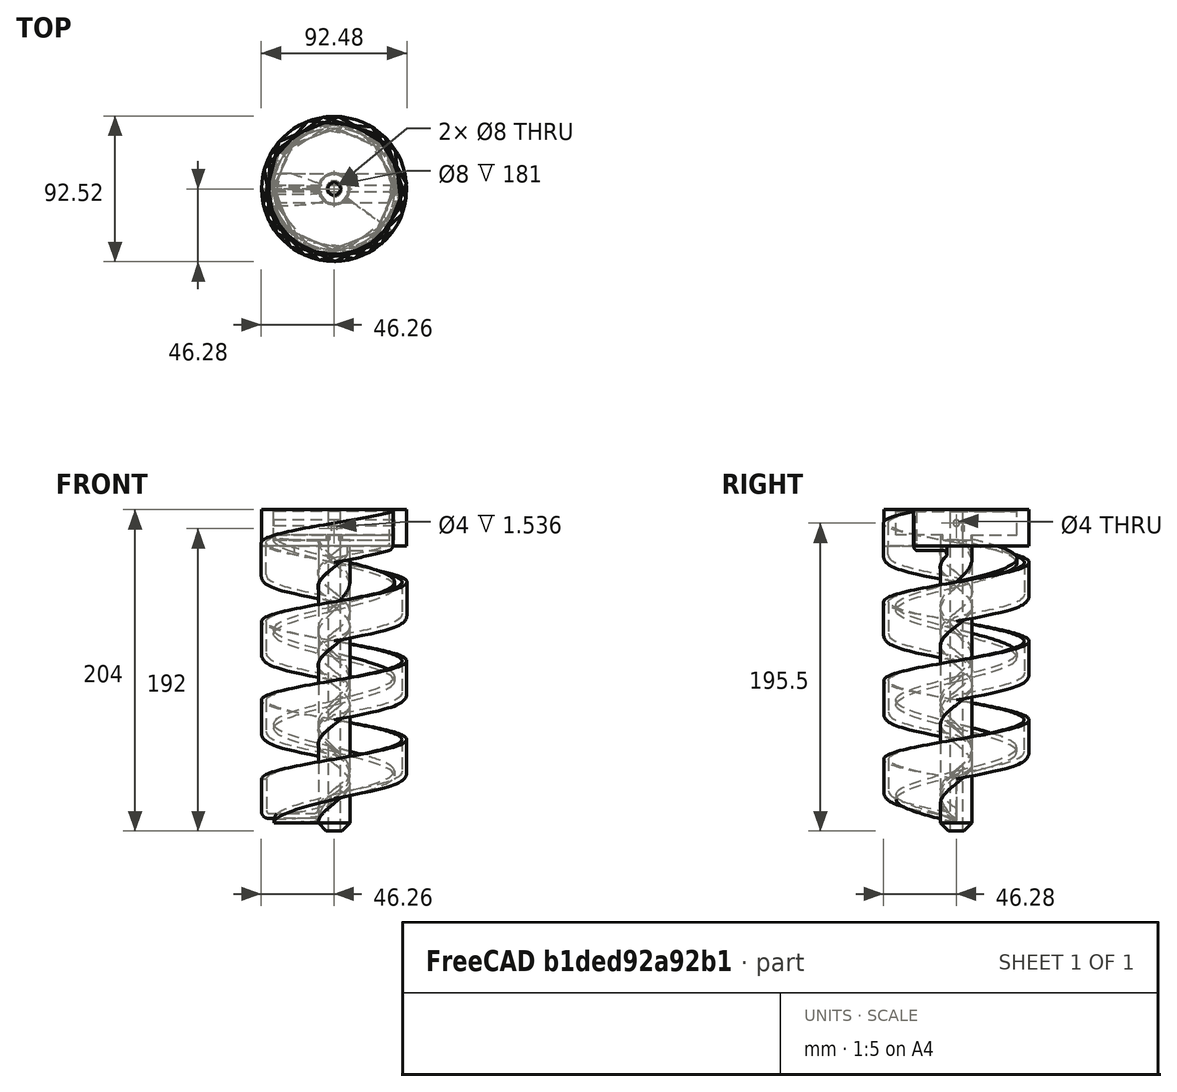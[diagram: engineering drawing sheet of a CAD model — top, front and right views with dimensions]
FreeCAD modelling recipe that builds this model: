
FCSTD DOCUMENT  (FreeCAD 1.1R14555 (Git shallow))
Label: Body - 1.3
License: All rights reserved
LicenseURL: https://en.wikipedia.org/wiki/All_rights_reserved
objects: Sketcher::SketchObject×12, PartDesign::Pad×6, PartDesign::Chamfer×5, PartDesign::Pocket×5, PartDesign::AdditiveHelix×2, PartDesign::Body×2, App::Point×2, PartDesign::Fillet×1
note: 83 computed .brp shape members not serialized (recipe doc carries the construction recipe); baked Part::Feature solids carry a one-line shape summary decoded from their .brp

FEATURE [Sketcher::SketchObject] Sketch
  ArcFitTolerance = 1e-06
  AttachmentSupport = -> [XY_Plane]
  ExternalTypes = [0]
  FullyConstrained = true
  MakeInternals = false
  MapMode = 5
  sketch-geometry (1):
    g0: Circle CenterX=0 CenterY=0 CenterZ=0 NormalX=0 NormalY=0 NormalZ=1 AngleXU=0 Radius=10
  constraints (2):
    c: Coincident(g0,g-1)
    c: Diameter(g0) = 20
FEATURE [PartDesign::Pad] Pad
  Direction = (0,0,1)
  Length = 200
  Length2 = 10
  Profile = -> Sketch
  ReferenceAxis = -> Sketch [N_Axis]
  Refine = true
  SideType = 0
  Suppressed = false
  Type = 0
  Type2 = 0
FEATURE [PartDesign::Chamfer] Chamfer
  Angle = 45
  Base = -> Pad [Edge2]
  BaseFeature = -> Pad
  ChamferType = 0
  FlipDirection = false
  Refine = true
  Size = 5
  Size2 = 1
  SupportTransform = false
  Suppressed = false
  UseAllEdges = false
FEATURE [Sketcher::SketchObject] Sketch001
  ArcFitTolerance = 1e-06
  AttachmentSupport = -> [XZ_Plane]
  ExternalGeometry = -> [Chamfer]
  ExternalTypes = [0]
  FullyConstrained = true
  MakeInternals = false
  MapMode = 5
  Placement = pos=(0,0,0) rot=(1,0,0;1.5708rad)
  expr: Constraints[11] = 77 / 2 - 0.3
  sketch-geometry (4):
    g0: LineSegment StartX=-38.2 StartY=8 StartZ=0 EndX=-38.2 EndY=5 EndZ=0
    g1: LineSegment StartX=-38.2 StartY=5 StartZ=0 EndX=0 EndY=5 EndZ=0
    g2: LineSegment StartX=0 StartY=5 StartZ=0 EndX=0 EndY=8 EndZ=0
    g3: LineSegment StartX=0 StartY=8 StartZ=0 EndX=-38.2 EndY=8 EndZ=0
  constraints (12):
    c: Coincident(g0,g1)
    c: Coincident(g1,g2)
    c: Coincident(g2,g3)
    c: Coincident(g3,g0)
    c: Vertical(g0)
    c: Vertical(g2)
    c: Horizontal(g1)
    c: Horizontal(g3)
    c: PointOnObject(g1,g-2)
    c: Horizontal(g0,g-3)
    c: DistanceY(g0,g0) = 3
    c: DistanceX(g1,g1) = 38.2
FEATURE [PartDesign::AdditiveHelix] AdditiveHelix
  Angle = 0.1
  Axis = (0,2e-16,1)
  Base = (0,0,0)
  BaseFeature = -> Chamfer
  Growth = 0.10472
  HasBeenEdited = true
  Height = 180
  LeftHanded = false
  Mode = 0
  Outside = false
  Pitch = 60
  Profile = -> Sketch001
  ReferenceAxis = -> Sketch001 [V_Axis]
  Refine = true
  Suppressed = false
  Tolerance = 0.1
  Turns = 3
FEATURE [Sketcher::SketchObject] Sketch002
  ArcFitTolerance = 1e-06
  AttachmentSupport = -> [Chamfer]
  ExternalTypes = [0]
  FullyConstrained = true
  MakeInternals = false
  MapMode = 5
  Placement = pos=(0,0,200) rot=(0,0,1;0rad)
  sketch-geometry (1):
    g0: Circle CenterX=0 CenterY=0 CenterZ=0 NormalX=0 NormalY=0 NormalZ=1 AngleXU=0 Radius=38.5
  constraints (2):
    c: Coincident(g0,g-1)
    c: Diameter(g0) = 77
FEATURE [PartDesign::Chamfer] Chamfer001
  Angle = 45
  Base = -> AdditiveHelix [Edge12]
  BaseFeature = -> AdditiveHelix
  ChamferType = 0
  FlipDirection = false
  Refine = true
  Size = 2.99
  Size2 = 1
  SupportTransform = false
  Suppressed = false
  UseAllEdges = false
FEATURE [PartDesign::Chamfer] Chamfer002
  Angle = 45
  Base = -> Chamfer001 [Edge12]
  BaseFeature = -> Chamfer001
  ChamferType = 0
  FlipDirection = false
  Refine = true
  Size = 4
  Size2 = 1
  SupportTransform = false
  Suppressed = false
  UseAllEdges = false
FEATURE [PartDesign::Chamfer] Chamfer003
  Angle = 45
  Base = -> Chamfer002 [Edge13]
  BaseFeature = -> Chamfer002
  ChamferType = 0
  FlipDirection = false
  Refine = true
  Size = 4
  Size2 = 1
  SupportTransform = false
  Suppressed = false
  UseAllEdges = false
FEATURE [PartDesign::Pad] Pad001
  BaseFeature = -> Chamfer003
  Direction = (0,0,1)
  Length = 3
  Length2 = 10
  Profile = -> Sketch002
  ReferenceAxis = -> Sketch002 [N_Axis]
  Refine = true
  SideType = 0
  Suppressed = false
  Type = 0
  Type2 = 0
FEATURE [Sketcher::SketchObject] Sketch003
  ArcFitTolerance = 1e-06
  AttachmentSupport = -> [Pad001]
  ExternalTypes = [0]
  FullyConstrained = true
  MakeInternals = false
  MapMode = 5
  Placement = pos=(0,0,200) rot=(1,0,0;3.14159rad)
  sketch-geometry (1):
    g0: Circle CenterX=0 CenterY=0 CenterZ=0 NormalX=0 NormalY=0 NormalZ=1 AngleXU=0 Radius=38.5
  constraints (2):
    c: Coincident(g0,g-1)
    c: Diameter(g0) = 77
FEATURE [PartDesign::Pad] Pad002
  BaseFeature = -> Pad001
  Direction = (0,0,-1)
  Length = 12
  Length2 = 10
  Profile = -> Sketch003
  ReferenceAxis = -> Sketch003 [N_Axis]
  Refine = true
  SideType = 0
  Suppressed = false
  Type = 0
  Type2 = 0
FEATURE [PartDesign::Fillet] Fillet
  Base = -> Pad002 [Edge36]
  BaseFeature = -> Pad002
  Radius = 3
  Refine = true
  SupportTransform = false
  Suppressed = false
  UseAllEdges = false
FEATURE [Sketcher::SketchObject] Sketch004
  ArcFitTolerance = 1e-06
  AttachmentSupport = -> [Fillet]
  ExternalTypes = [0]
  FullyConstrained = true
  MakeInternals = false
  MapMode = 5
  Placement = pos=(0,0,203) rot=(0,0,1;0rad)
  sketch-geometry (2):
    g0: Circle CenterX=0 CenterY=0 CenterZ=0 NormalX=0 NormalY=0 NormalZ=1 AngleXU=0 Radius=38.5
    g1: Circle CenterX=0 CenterY=0 CenterZ=0 NormalX=0 NormalY=0 NormalZ=1 AngleXU=0 Radius=50
  constraints (4):
    c: Coincident(g0,g-1)
    c: Diameter(g0) = 77
    c: Coincident(g1,g0)
    c: Diameter(g1) = 100
FEATURE [PartDesign::Pocket] Pocket
  BaseFeature = -> Fillet
  Direction = (0,0,-1)
  Length = 180
  Length2 = 5
  Profile = -> Sketch004
  ReferenceAxis = -> Sketch004 [N_Axis]
  Refine = true
  Reversed = true
  SideType = 0
  Suppressed = false
  Type = 0
  Type2 = 0
FEATURE [Sketcher::SketchObject] Sketch005
  ArcFitTolerance = 1e-06
  AttachmentSupport = -> [YZ_Plane]
  ExternalGeometry = -> [Pocket]
  ExternalTypes = [0]
  FullyConstrained = true
  MakeInternals = false
  MapMode = 5
  Placement = pos=(0,0,0) rot=(0.57735,0.57735,0.57735;2.0944rad)
  sketch-geometry (1):
    g0: Circle CenterX=9.4e-15 CenterY=195.5 CenterZ=0 NormalX=0 NormalY=0 NormalZ=1 AngleXU=0 Radius=2
  constraints (3):
    c: PointOnObject(g0,g-3)
    c: Diameter(g0) = 4
    c: Symmetric(g-3,g-3,g0)
FEATURE [PartDesign::Pocket] Pocket001
  BaseFeature = -> Pocket
  Direction = (-1,0,0)
  Length = 500
  Length2 = 5
  Profile = -> Sketch005
  ReferenceAxis = -> Sketch005 [N_Axis]
  Refine = true
  Reversed = true
  SideType = 0
  Suppressed = false
  Type = 0
  Type2 = 0
FEATURE [PartDesign::Pocket] Pocket002
  BaseFeature = -> Pocket001
  Direction = (-1,0,0)
  Length = 5
  Length2 = 5
  Profile = -> Pocket001 [Face21]
  Refine = true
  SideType = 0
  Suppressed = false
  Type = 1
  Type2 = 0
FEATURE [Sketcher::SketchObject] Sketch006
  ArcFitTolerance = 1e-06
  AttachmentSupport = -> [YZ_Plane]
  ExternalTypes = [0]
  FullyConstrained = false
  MakeInternals = false
  MapMode = 5
  Placement = pos=(0,0,0) rot=(0.57735,0.57735,0.57735;2.0944rad)
  sketch-geometry (4):
    g0: LineSegment StartX=9.56195 StartY=192.563 StartZ=0 EndX=-8.62475 EndY=192.563 EndZ=0
    g1: LineSegment StartX=-8.62475 StartY=192.563 StartZ=0 EndX=-8.62475 EndY=184.759 EndZ=0
    g2: LineSegment StartX=-8.62475 StartY=184.759 StartZ=0 EndX=9.56195 EndY=184.759 EndZ=0
    g3: LineSegment StartX=9.56195 StartY=184.759 StartZ=0 EndX=9.56195 EndY=192.563 EndZ=0
  constraints (8):
    c: Coincident(g0,g1)
    c: Coincident(g1,g2)
    c: Coincident(g2,g3)
    c: Coincident(g3,g0)
    c: Horizontal(g0)
    c: Horizontal(g2)
    c: Vertical(g1)
    c: Vertical(g3)
FEATURE [PartDesign::Pad] Pad003
  BaseFeature = -> Pocket002
  Direction = (1,0,0)
  Length = 50
  Length2 = 50
  Profile = -> Sketch006
  ReferenceAxis = -> Sketch006 [N_Axis]
  Refine = true
  SideType = 0
  Suppressed = false
  Type = 4
  Type2 = 0
FEATURE [Sketcher::SketchObject] Sketch007
  ArcFitTolerance = 1e-06
  AttachmentSupport = -> [Pad003]
  ExternalTypes = [0]
  FullyConstrained = true
  MakeInternals = false
  MapMode = 5
  Placement = pos=(0,0,203) rot=(0,0,1;0rad)
  sketch-geometry (2):
    g0: Circle CenterX=0 CenterY=0 CenterZ=0 NormalX=0 NormalY=0 NormalZ=1 AngleXU=0 Radius=38.5
    g1: Circle CenterX=0 CenterY=0 CenterZ=0 NormalX=0 NormalY=0 NormalZ=1 AngleXU=0 Radius=55
  constraints (4):
    c: Coincident(g0,g-1)
    c: Diameter(g0) = 77
    c: Diameter(g1) = 110
    c: Coincident(g1,g0)
FEATURE [PartDesign::Pocket] Pocket003
  BaseFeature = -> Pad003
  Direction = (0,0,-1)
  Length = 30
  Length2 = 5
  Profile = -> Sketch007
  ReferenceAxis = -> Sketch007 [N_Axis]
  Refine = true
  SideType = 0
  Suppressed = false
  Type = 0
  Type2 = 0
FEATURE [PartDesign::Body] Body
  AllowCompound = false
  Group = -> [Sketch,Pad,Chamfer,Sketch001,AdditiveHelix,Sketch002,Chamfer001,Chamfer002,Chamfer003,Pad001,Sketch003,Pad002,Fillet,Sketch004,Pocket,Sketch005,Pocket001,Pocket002,Sketch006,Pad003,Sketch007,Pocket003]
  Origin = -> Origin
  Tip = -> Pocket003
FEATURE [Sketcher::SketchObject] Sketch008
  ArcFitTolerance = 1e-06
  AttachmentSupport = -> [XY_Plane001]
  ExternalTypes = [0]
  FullyConstrained = true
  MakeInternals = false
  MapMode = 5
  sketch-geometry (2):
    g0: Circle CenterX=0 CenterY=0 CenterZ=0 NormalX=0 NormalY=0 NormalZ=1 AngleXU=0 Radius=10
    g1: Circle CenterX=0 CenterY=0 CenterZ=0 NormalX=0 NormalY=0 NormalZ=1 AngleXU=0 Radius=4
  constraints (4):
    c: Coincident(g0,g-1)
    c: Diameter(g0) = 20
    c: Coincident(g1,g0)
    c: Diameter(g1) = 8
FEATURE [PartDesign::Pad] Pad004
  Direction = (0,0,1)
  Length = 200
  Length2 = 10
  Profile = -> Sketch008
  ReferenceAxis = -> Sketch008 [N_Axis]
  Refine = true
  SideType = 0
  Suppressed = false
  Type = 0
  Type2 = 0
FEATURE [PartDesign::Chamfer] Chamfer004
  Angle = 45
  Base = -> Pad004 [Edge2]
  BaseFeature = -> Pad004
  ChamferType = 0
  FlipDirection = false
  Refine = true
  Size = 5
  Size2 = 1
  SupportTransform = false
  Suppressed = false
  UseAllEdges = false
FEATURE [Sketcher::SketchObject] Sketch009
  ArcFitTolerance = 1e-06
  AttachmentSupport = -> [XZ_Plane001]
  ExternalGeometry = -> [Chamfer004]
  ExternalTypes = [0]
  FullyConstrained = true
  MakeInternals = false
  MapMode = 5
  Placement = pos=(0,0,0) rot=(1,0,0;1.5708rad)
  sketch-geometry (13):
    g0: LineSegment StartX=-13 StartY=11 StartZ=0 EndX=-41 EndY=11 EndZ=0
    g1: LineSegment StartX=-46 StartY=12 StartZ=0 EndX=-46 EndY=33 EndZ=0
    g2: LineSegment StartX=-43 StartY=33 StartZ=0 EndX=-43 EndY=13 EndZ=0
    g3: ArcOfCircle CenterX=-41 CenterY=13 CenterZ=0 NormalX=0 NormalY=0 NormalZ=1 AngleXU=0 Radius=2 StartAngle=3.14159 EndAngle=4.71239
    g4: GeomPoint [constr] X=-43 Y=11 Z=0
    g5: ArcOfCircle CenterX=-42 CenterY=12 CenterZ=0 NormalX=0 NormalY=0 NormalZ=1 AngleXU=0 Radius=4 StartAngle=3.14159 EndAngle=4.71239
    g6: ArcOfCircle CenterX=-13 CenterY=14 CenterZ=0 NormalX=0 NormalY=0 NormalZ=1 AngleXU=0 Radius=3 StartAngle=4.71239 EndAngle=6.28319
    g7: LineSegment StartX=-10 StartY=14 StartZ=0 EndX=-8 EndY=14 EndZ=0
    g8: LineSegment StartX=-8 StartY=14 StartZ=0 EndX=-8 EndY=5 EndZ=0
    g9: LineSegment StartX=-46 StartY=33 StartZ=0 EndX=-43 EndY=33 EndZ=0
    g10: LineSegment StartX=-42 StartY=8 StartZ=0 EndX=-13 EndY=8 EndZ=0
    g11: ArcOfCircle CenterX=-13 CenterY=5 CenterZ=0 NormalX=0 NormalY=0 NormalZ=1 AngleXU=0 Radius=3 StartAngle=1e-16 EndAngle=1.5708
    g12: LineSegment StartX=-10 StartY=5 StartZ=0 EndX=-8 EndY=5 EndZ=0
  constraints (38):
    c: Vertical(g1)
    c: Vertical(g2)
    c: PointOnObject(g4,g0)
    c: PointOnObject(g4,g2)
    c: Tangent(g0,g3) = 1.5708
    c: Tangent(g2,g3) = -1.5708
    c: Tangent(g1,g5) = 1.5708
    c: DistanceY(g2,g2) = 20
    c: Radius(g3) = 2
    c: Radius(g5) = 4
    c: Horizontal(g0)
    c: DistanceX(g1,g-1) = 46
    c: Coincident(g6,g0)
    c: Vertical(g6,g0)
    c: Radius(g6) = 3
    c: Horizontal(g6,g6)
    c: DistanceY(g5,g0) = 3
    c: Coincident(g7,g6)
    c: Coincident(g8,g7)
    c: Vertical(g8)
    c: Horizontal(g7)
    c: Distance(g7,g7) = 2
    c: Horizontal(g1,g2)
    c: DistanceX(g1,g2) = 3
    c: Coincident(g9,g1)
    c: Coincident(g9,g2)
    c: Vertical(g6,g-3)
    c: Vertical(g5,g5)
    c: Coincident(g10,g5)
    c: Horizontal(g10)
    c: Coincident(g11,g10)
    c: Coincident(g11,g-3)
    c: Vertical(g10,g11)
    c: Horizontal(g11,g11)
    c: Coincident(g12,g11)
    c: Coincident(g12,g8)
    c: Horizontal(g12)
    c: Equal(g6,g11)
FEATURE [PartDesign::AdditiveHelix] AdditiveHelix001
  Angle = 0.1
  Axis = (0,2e-16,1)
  Base = (0,0,0)
  BaseFeature = -> Chamfer004
  Growth = 0.0872666
  HasBeenEdited = true
  Height = 170
  LeftHanded = false
  Mode = 0
  Outside = false
  Pitch = 50
  Profile = -> Sketch009
  ReferenceAxis = -> Sketch009 [V_Axis]
  Refine = true
  Suppressed = false
  Tolerance = 0.1
  Turns = 3.4
FEATURE [App::Point] Origin002  label="Origin"
  Role = Origin
FEATURE [App::Point] Origin003  label="Origin"
  Role = Origin
FEATURE [Sketcher::SketchObject] Sketch010
  ArcFitTolerance = 1e-06
  AttachmentSupport = -> [AdditiveHelix001]
  ExternalTypes = [0]
  FullyConstrained = true
  MakeInternals = false
  MapMode = 5
  Placement = pos=(0,0,200) rot=(0,0,1;0rad)
  expr: Constraints[3] = 2 * 46
  sketch-geometry (2):
    g0: Circle CenterX=0 CenterY=0 CenterZ=0 NormalX=0 NormalY=0 NormalZ=1 AngleXU=0 Radius=4
    g1: Circle CenterX=0 CenterY=0 CenterZ=0 NormalX=0 NormalY=0 NormalZ=1 AngleXU=0 Radius=46
  constraints (4):
    c: Coincident(g0,g-1)
    c: Coincident(g1,g0)
    c: Diameter(g0) = 8
    c: Diameter(g1) = 92
FEATURE [PartDesign::Pad] Pad005
  BaseFeature = -> AdditiveHelix001
  Direction = (0,0,1)
  Length = 19
  Length2 = 4
  Profile = -> Sketch010
  ReferenceAxis = -> Sketch010 [N_Axis]
  Reversed = true
  SideType = 1
  Suppressed = false
  Type = 0
  Type2 = 0
FEATURE [Sketcher::SketchObject] Sketch011
  ArcFitTolerance = 1e-06
  AttachmentSupport = -> [Origin001]
  ExternalTypes = [0]
  FullyConstrained = true
  MakeInternals = false
  MapMode = 5
  Placement = pos=(0,0,0) rot=(1,0,0;1.5708rad)
  sketch-geometry (1):
    g0: Circle CenterX=0 CenterY=192 CenterZ=0 NormalX=0 NormalY=0 NormalZ=1 AngleXU=0 Radius=2
  constraints (3):
    c: PointOnObject(g0,g-2)
    c: Diameter(g0) = 4
    c: Distance(g0,g-1) = 192
FEATURE [PartDesign::Pocket] Pocket004
  BaseFeature = -> Pad005
  Direction = (0,1,-2e-16)
  Length = 5
  Length2 = 5
  Profile = -> Sketch011
  ReferenceAxis = -> Sketch011 [N_Axis]
  SideType = 0
  Suppressed = false
  Type = 0
  Type2 = 0
FEATURE [PartDesign::Body] Body001
  AllowCompound = false
  Group = -> [Sketch008,Pad004,Chamfer004,Sketch009,AdditiveHelix001,Sketch010,Pad005,Sketch011,Pocket004]
  Origin = -> Origin001
  Tip = -> Pocket004
